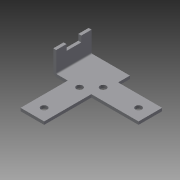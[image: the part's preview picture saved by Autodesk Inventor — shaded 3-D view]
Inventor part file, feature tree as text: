
AUTODESK INVENTOR PART (.ipt)
format: ipt  version: 2013 (Build 170138000, 138)  size: 108,032 bytes
history: native  units: in
note: dims shown in document units (in); Inventor stores cm internally (conversion verified against a paired STEP export)
features: sketch x2, other x2, sheet_metal_op x1
ambient origin geometry x8: Origin, YZ Plane, XZ Plane, XY Plane, X Axis, Y Axis, Z Axis, Center Point
bodies: Solid1 (feature_tree)
feature tree (5):
  sheet_metal_op  "Face1"
  sketch  "Sketch1"  dims[d1=0.125in]
  other  "Plate1"
  sketch  "Sketch7"  dims[d32=0.615in d44=2.0in d45=0.125in d46=0.0in]
  other  "Cut3"
